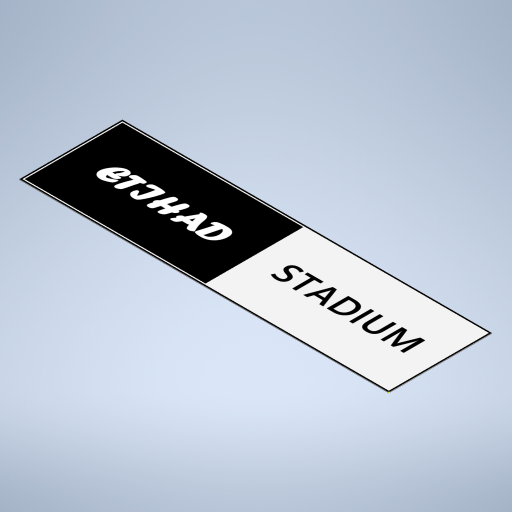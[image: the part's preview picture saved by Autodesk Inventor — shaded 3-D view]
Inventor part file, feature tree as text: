
AUTODESK INVENTOR PART (.ipt)
format: ipt  version: 2024.1 (Build 281209000, 209)  size: 272,896 bytes
history: native  units: in
note: dims shown in document units (in); Inventor stores cm internally (conversion verified against a paired STEP export)
features: sketch x3, extrude x3
ambient origin geometry x8: Origin, YZ Plane, XZ Plane, XY Plane, X Axis, Y Axis, Z Axis, Center Point
bodies: Solid6 (feature_tree), Solid7 (feature_tree)
feature tree (6):
  sketch  "Sketch2"  dims[d20=5.0in d21=0.0in d22=5.0in d23=0.0in]
  extrude  "Extrusion5"  Depth=5.0in TaperAngle=0.0deg
  extrude  "Extrusion6"  Depth=5.0in
  extrude  "Extrusion7"  Depth=0.5in
  sketch  "Sketch3"  dims[d24=5.0in d25=0.0in d7=0.5in]
  sketch  "Sketch4"  dims[d8=0.0344in d9=0.5in d10=0.0344in]
